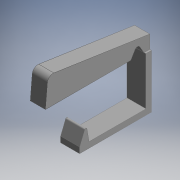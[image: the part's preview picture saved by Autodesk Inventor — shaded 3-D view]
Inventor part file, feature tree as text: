
AUTODESK INVENTOR PART (.ipt)
format: ipt  version: 2018 (Build 220112000, 112)  size: 157,184 bytes
history: native  units: mm
features: extrude x5, other x5, fillet x2
ambient origin geometry x8: Origin, YZ Plane, XZ Plane, XY Plane, X Axis, Y Axis, Z Axis, Center Point
bodies: Solid1 (feature_tree)
feature tree (12):
  extrude  "Key"  Depth=55.0mm
  fillet  "Key Front Rounding"  Radius=15.0mm
  extrude  "Downward Lever Section"  Depth=7.0mm
  extrude  "Horizontal Lever Section"  TaperAngle=0.0deg  [1 undecoded]
  extrude  "Hinge Cut"  Depth=3.0mm
  extrude  "Tube Pincher"  Depth=14.835299mm
  fillet  "Tube Pincher Rounding"  [1 undecoded]
  other  "Key Sketch"
  other  "Down Lever Sect Sketch"
  other  "Hinge Cut Sketch"
  other  "Horiz Lever Sect Sketch"
  other  "Tube Pincher Sketch"
note: 2 required parameter values undecoded (feature->parameter linkage not recoverable at this tier; creation-order binding heuristic only, values carry confidence <= 0.55)
